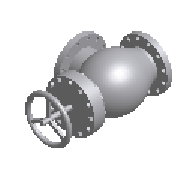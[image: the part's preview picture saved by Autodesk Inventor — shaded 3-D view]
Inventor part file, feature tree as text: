
AUTODESK INVENTOR PART (.ipt)
format: ipt  version: 2024 (Build 280153000, 153)  size: 343,040 bytes
history: native  units: mm (DEFAULTED — no unit token found)
features: other x8, extrude x5, pattern_circular x3, revolve x2, plane x1
ambient origin geometry x8: Origin, YZ Plane, XZ Plane, XY Plane, X Axis, Y Axis, Z Axis, Center Point
bodies: Body1 (feature_tree)
feature tree (19):
  revolve  "Revolution1"  [1 undecoded]
  extrude  "Extrusion1"  Depth=123.952mm
  pattern_circular  "Circular Pattern1"  [2 undecoded]
  revolve  "Revolution2"  [1 undecoded]
  extrude  "Extrusion3"  Depth=35.052mm
  plane  "Work Plane1"
  extrude  "Extrusion4"  TaperAngle=90.0deg  [1 undecoded]
  pattern_circular  "Circular Pattern2"  [2 undecoded]
  extrude  "Extrusion5"  Depth=19.05mm
  extrude  "Extrusion6"  Depth=25.4mm TaperAngle=0.0deg
  pattern_circular  "Circular Pattern4"  Count=4  [1 undecoded]
  other  "Work Axis2"
  other  "Work Point1"
  other  "Work Axis3"
  other  "Work Point2"
  other  "Suprimir cara1"
  other  "Suprimir cara2"
  other  "Suprimir cara3"
  other  "Suprimir cara4"
note: 8 required parameter values undecoded (feature->parameter linkage not recoverable at this tier; creation-order binding heuristic only, values carry confidence <= 0.55)